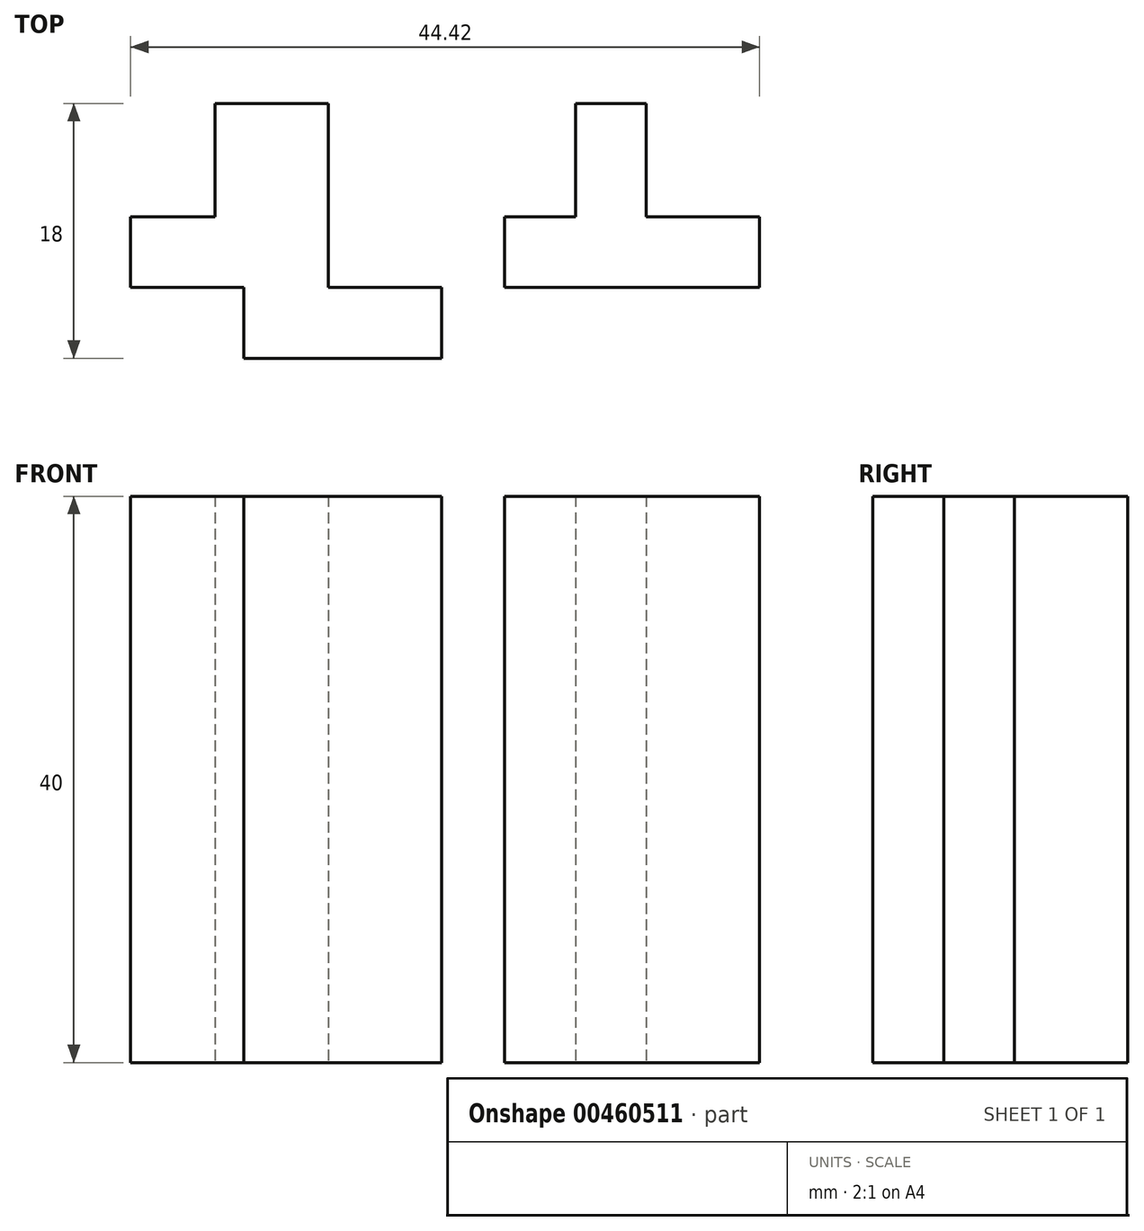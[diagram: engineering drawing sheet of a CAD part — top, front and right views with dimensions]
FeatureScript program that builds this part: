
annotation { "Feature Type Name" : "Feature", "Feature Type Description" : "" }
export const myFeature = defineFeature(function(context is Context, id is Id, definition is map)
    precondition{}
    {
        {
            var Q0;
            Q0=qCreatedBy(makeId("Top.planeOp"),FACE);
            var sketch = newSketch(context, id + "F0", { "sketchPlane" : qUnion([Q0])});
            skLineSegment(sketch, "E0.bottom", {"start": v(0, 0) * mm, "end": v(-18, 0) * mm});
            skLineSegment(sketch, "E0.top", {"start": v(0, 5) * mm, "end": v(-8, 5) * mm});
            skLineSegment(sketch, "E0.left", {"start": v(0, 0) * mm, "end": v(0, 5) * mm});
            skLineSegment(sketch, "E0.right", {"start": v(-18, 0) * mm, "end": v(-18, 5) * mm});
            skLineSegment(sketch, "E1", {"start": v(-8, 5) * mm, "end": v(-8, 13) * mm});
            skLineSegment(sketch, "E2", {"start": v(-8, 13) * mm, "end": v(-13, 13) * mm});
            skLineSegment(sketch, "E3", {"start": v(-13, 13) * mm, "end": v(-13, 5) * mm});
            skLineSegment(sketch, "E4.trimOffspring", {"start": v(-13, 5) * mm, "end": v(-18, 5) * mm});
            skLineSegment(sketch, "E5.top", {"start": v(-22.45, 0) * mm, "end": v(-30.45, 0) * mm});
            skLineSegment(sketch, "E5.left", {"start": v(-22.45, -5) * mm, "end": v(-22.45, 0) * mm});
            skLineSegment(sketch, "E6", {"start": v(-30.45, 0) * mm, "end": v(-30.45, 13) * mm});
            skLineSegment(sketch, "E7", {"start": v(-30.45, 13) * mm, "end": v(-38.45, 13) * mm});
            skLineSegment(sketch, "E8", {"start": v(-38.45, 13) * mm, "end": v(-38.45, 5) * mm});
            skLineSegment(sketch, "E9", {"start": v(-38.45, 5) * mm, "end": v(-44.42, 5) * mm});
            skLineSegment(sketch, "E10", {"start": v(-44.42, 5) * mm, "end": v(-44.42, 0) * mm});
            skLineSegment(sketch, "E11", {"start": v(-44.42, 0) * mm, "end": v(-36.42, 0) * mm});
            skLineSegment(sketch, "E12", {"start": v(-36.42, 0) * mm, "end": v(-36.42, -5) * mm});
            skLineSegment(sketch, "E13", {"start": v(-36.42, -5) * mm, "end": v(-22.45, -5) * mm});
            skSolve(sketch);
        }
        {
            var Q0;
            Q0=makeQuery(id+"F0.imprint","IMPRINT",FACE,{"disambiguationData":[TD([[makeQuery(id+"F0.imprint","IMPRINT",EDGE,{"derivedFrom":sQuery(id+"F0.wireOp",EDGE,"E0.bottom")}),-1.0]])]});
            var Q1;
            Q1=makeQuery(id+"F0.imprint","IMPRINT",FACE,{"disambiguationData":[TD([[makeQuery(id+"F0.imprint","IMPRINT",EDGE,{"derivedFrom":sQuery(id+"F0.wireOp",EDGE,"E5.top")}),1.0]])]});
            extrude(context, id + "F1", {"entities" : qUnion([Q0, Q1]), "depth" : 40 * mm});
        }
    });
